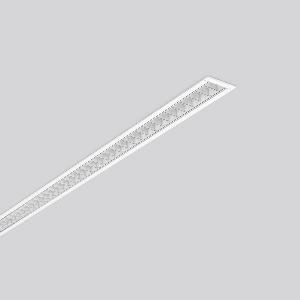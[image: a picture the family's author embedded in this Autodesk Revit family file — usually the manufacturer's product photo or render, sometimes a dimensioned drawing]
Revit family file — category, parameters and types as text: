
# Revit family: less_is_more_27_312177_002_2acf
name_source: partatom
category: Lighting Fixtures
units: mm (PartAtom-declared; Revit-internal decimal feet)

## family parameters
Cut with Voids When Loaded = No
Host = Face
Light Source = No
Part Type = Normal
Room Calculation Point = No
Round Connector Dimension = Use Diameter
Shared = No

## types (1)
- LESS IS MORE 27 (1 x LED Modul 830, 2350 lm, 3000)
    Apparent Load = 29 VA
    CIE Flux Codes = 90 99 100 100 100
    Color Rendering = 80
    Color Temperature = 3000
    Default Elevation = 1800 mm
    Description = Series: LESS IS MORE 27
Recessed ceiling and wall luminaire with slim design. Housing: extruded aluminium profile, powder-coated. End cap aluminium powder-coated. High polish aluminium micro grid. Perfect for office areas (RUG < 19) and environments with computer screens in accordance with EN 12464-1. Suitable for Recessed ceiling mounting, wall (recessed). External driver with connecting cable. 
Colour: traffic white, matt (RAL 9016)
Length: 1014 mm
Width: 38 mm
Height: 2 mm
Cut-out length: 1006 mm
Cut-out width: 30 mm
Recess height: 45-60 mm
Luminaire: recess height: 37 mm
Lamp: LED
Socket: without socket
Colour temperature: 3000K
Colour rendering index (CRI): 82
System power: 29 W
Rated luminous flux: 2350 lm
Luminous efficiency: 81 lm/W
Control gear: Regulated power supply
Protection class: II
Type of protection: IP 20
    Height = 0 mm  [stored 0 ft]
    Lamp = 1 x LED Modul 830
    Lamp Light Flux = 2350 lm
    Lamp count = 1
    Length = 1014 mm
    Lifetime = 50000 h
    Luminous efficacy = 81 lm/W
    Manufacturer = RZB
    ModVariant = No
    Model = 312177.002
    Mounting Place = Ceiling, Wall
    Mounting Type = Recessed
    Number of Poles = 1
    OnlyDefault = Yes
    Power Factor = 1
    Product Name = LESS IS MORE 27
    Product group = Recessed LED linear luminaires
    ProductGroupID = 407
    Protection Class = Protection class II
    Protection Degree = IP 20
    RLX_Detail_Level = 1
    RLX_Emergency_Light_Flux = 0 lm
    RLX_Emergency_Type = 0
    RLX_Emergency_Type_DB = No
    RlxData = <blob elided: 27013 chars, md5=0136b8dd>
    Socket = socket
    Standby Power = 0 W
    System Light Flux = 2350 lm
    System Power = 29 W
    Type Comments = Product without accessories
    Type Image = 312177.002.jpg
    URL = http://relux.com
    VarID = ---
    Voltage = 230 V
    Voltage Range = 220-240 V
    Weight = 0.00 kg
    Width = 38 mm

note: [stored X ft] marks values corroborated as IEEE doubles in the binary element streams (Revit-internal decimal feet)

## geometry (parser evidence)
native form markers: Blend x4, Sweep x11
no freeform markers — native parametric forms only
